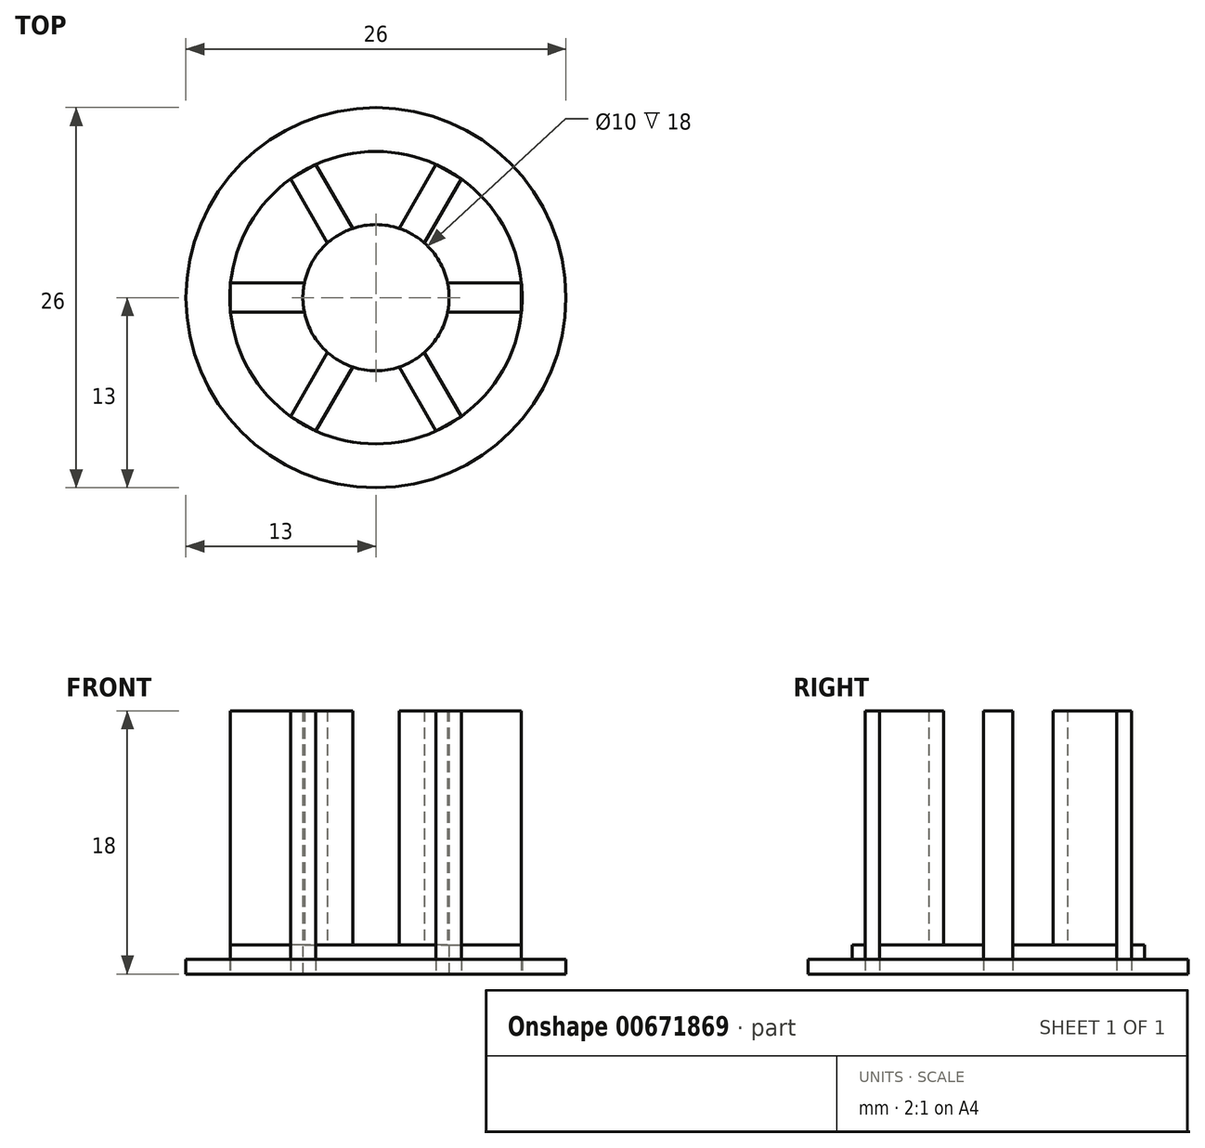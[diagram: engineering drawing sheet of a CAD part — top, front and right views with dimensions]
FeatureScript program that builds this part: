
annotation { "Feature Type Name" : "Feature", "Feature Type Description" : "" }
export const myFeature = defineFeature(function(context is Context, id is Id, definition is map)
    precondition{}
    {
        {
            var Q0;
            Q0=qCreatedBy(makeId("Top.planeOp"),FACE);
            var sketch = newSketch(context, id + "F0", { "sketchPlane" : qUnion([Q0])});
            skCircle(sketch, "E0", {"center": v(0, 0) * mm, "radius": 10 * mm});
            skCircle(sketch, "E1", {"center": v(0, 0) * mm, "radius": 13 * mm});
            skCircle(sketch, "E2", {"center": v(0, 0) * mm, "radius": 5 * mm});
            skLineSegment(sketch, "E3.bottom", {"start": v(9.95, -1) * mm, "end": v(4.9, -1) * mm});
            skLineSegment(sketch, "E3.top", {"start": v(9.95, 1) * mm, "end": v(4.9, 1) * mm});
            skLineSegment(sketch, "E3.left", {"start": v(9.95, -1) * mm, "end": v(9.95, 1) * mm});
            skLineSegment(sketch, "E3.right", {"start": v(4.9, -1) * mm, "end": v(4.9, 1) * mm});
            skPoint(sketch, "E3.middle", {"position": v(7.42, 0) * mm});
            skLineSegment(sketch, "E4.1.0", {"start": v(4.1, 9.12) * mm, "end": v(1.58, 4.74) * mm});
            skLineSegment(sketch, "E4.1.1", {"start": v(3.31, 3.74) * mm, "end": v(1.58, 4.74) * mm});
            skLineSegment(sketch, "E4.1.2", {"start": v(5.84, 8.12) * mm, "end": v(3.31, 3.74) * mm});
            skLineSegment(sketch, "E4.1.3", {"start": v(5.84, 8.12) * mm, "end": v(4.1, 9.12) * mm});
            skLineSegment(sketch, "E4.2.0", {"start": v(-5.84, 8.12) * mm, "end": v(-3.31, 3.74) * mm});
            skLineSegment(sketch, "E4.2.1", {"start": v(-1.58, 4.74) * mm, "end": v(-3.31, 3.74) * mm});
            skLineSegment(sketch, "E4.2.2", {"start": v(-4.1, 9.12) * mm, "end": v(-1.58, 4.74) * mm});
            skLineSegment(sketch, "E4.2.3", {"start": v(-4.1, 9.12) * mm, "end": v(-5.84, 8.12) * mm});
            skLineSegment(sketch, "E4.3.0", {"start": v(-9.95, -1) * mm, "end": v(-4.9, -1) * mm});
            skLineSegment(sketch, "E4.3.1", {"start": v(-4.9, 1) * mm, "end": v(-4.9, -1) * mm});
            skLineSegment(sketch, "E4.3.2", {"start": v(-9.95, 1) * mm, "end": v(-4.9, 1) * mm});
            skLineSegment(sketch, "E4.3.3", {"start": v(-9.95, 1) * mm, "end": v(-9.95, -1) * mm});
            skLineSegment(sketch, "E4.4.0", {"start": v(-4.1, -9.12) * mm, "end": v(-1.58, -4.74) * mm});
            skLineSegment(sketch, "E4.4.1", {"start": v(-3.31, -3.74) * mm, "end": v(-1.58, -4.74) * mm});
            skLineSegment(sketch, "E4.4.2", {"start": v(-5.84, -8.12) * mm, "end": v(-3.31, -3.74) * mm});
            skLineSegment(sketch, "E4.4.3", {"start": v(-5.84, -8.12) * mm, "end": v(-4.1, -9.12) * mm});
            skLineSegment(sketch, "E4.5.0", {"start": v(5.84, -8.12) * mm, "end": v(3.31, -3.74) * mm});
            skLineSegment(sketch, "E4.5.1", {"start": v(1.58, -4.74) * mm, "end": v(3.31, -3.74) * mm});
            skLineSegment(sketch, "E4.5.2", {"start": v(4.1, -9.12) * mm, "end": v(1.58, -4.74) * mm});
            skLineSegment(sketch, "E4.5.3", {"start": v(4.1, -9.12) * mm, "end": v(5.84, -8.12) * mm});
            skSolve(sketch);
        }
        {
            var Q0;
            Q0=makeQuery(id+"F0.imprint","IMPRINT",FACE,{"disambiguationData":[TD([[makeQuery(id+"F0.imprint","IMPRINT",EDGE,{"derivedFrom":sQuery(id+"F0.wireOp",EDGE,"E1")}),1.0]])]});
            extrude(context, id + "F1", {"entities" : qUnion([Q0]), "depth" : 1 * mm, "offsetDistance" : 25 * mm});
        }
        {
            var Q0;
            {var subQ0=sQuery(id+"F0.wireOp",EDGE,"E4.3.0");var subQ5=sQuery(id+"F0.wireOp",EDGE,"E2");var subQ6=makeQuery(id+"F0.imprint","INTERSECT",VERTEX,{"derivedFrom":[subQ5,subQ0]});Q0=makeQuery(id+"F0.imprint","IMPRINT",FACE,{"disambiguationData":[TD([[makeQuery(id+"F0.imprint","IMPRINT",EDGE,{"disambiguationData":[TD([[subQ6,-1.0]])],"derivedFrom":subQ5}),-1.0]])]});}
            var Q1;
            {var subQ5=sQuery(id+"F0.wireOp",EDGE,"E4.3.3");Q1=makeQuery(id+"F0.imprint","IMPRINT",FACE,{"disambiguationData":[TD([[makeQuery(id+"F0.imprint","IMPRINT",EDGE,{"derivedFrom":subQ5}),1.0]])]});}
            var Q2;
            {var subQ0=sQuery(id+"F0.wireOp",EDGE,"E4.2.0");var subQ5=sQuery(id+"F0.wireOp",EDGE,"E2");var subQ6=makeQuery(id+"F0.imprint","INTERSECT",VERTEX,{"derivedFrom":[subQ5,subQ0]});Q2=makeQuery(id+"F0.imprint","IMPRINT",FACE,{"disambiguationData":[TD([[makeQuery(id+"F0.imprint","IMPRINT",EDGE,{"disambiguationData":[TD([[subQ6,-1.0]])],"derivedFrom":subQ5}),-1.0]])]});}
            var Q3;
            {var subQ5=sQuery(id+"F0.wireOp",EDGE,"E4.2.3");Q3=makeQuery(id+"F0.imprint","IMPRINT",FACE,{"disambiguationData":[TD([[makeQuery(id+"F0.imprint","IMPRINT",EDGE,{"derivedFrom":subQ5}),1.0]])]});}
            var Q4;
            {var subQ0=sQuery(id+"F0.wireOp",EDGE,"E4.1.0");var subQ5=sQuery(id+"F0.wireOp",EDGE,"E2");var subQ6=makeQuery(id+"F0.imprint","INTERSECT",VERTEX,{"derivedFrom":[subQ5,subQ0]});Q4=makeQuery(id+"F0.imprint","IMPRINT",FACE,{"disambiguationData":[TD([[makeQuery(id+"F0.imprint","IMPRINT",EDGE,{"disambiguationData":[TD([[subQ6,-1.0]])],"derivedFrom":subQ5}),-1.0]])]});}
            var Q5;
            {var subQ3=sQuery(id+"F0.wireOp",EDGE,"E4.1.2");var subQ5=sQuery(id+"F0.wireOp",EDGE,"E2");var subQ6=makeQuery(id+"F0.imprint","INTERSECT",VERTEX,{"derivedFrom":[subQ5,subQ3]});Q5=makeQuery(id+"F0.imprint","IMPRINT",FACE,{"disambiguationData":[TD([[makeQuery(id+"F0.imprint","IMPRINT",EDGE,{"disambiguationData":[TD([[subQ6,1.0]])],"derivedFrom":subQ5}),-1.0]])]});}
            var Q6;
            {var subQ5=sQuery(id+"F0.wireOp",EDGE,"E3.left");Q6=makeQuery(id+"F0.imprint","IMPRINT",FACE,{"disambiguationData":[TD([[makeQuery(id+"F0.imprint","IMPRINT",EDGE,{"derivedFrom":subQ5}),1.0]])]});}
            var Q7;
            {var subQ5=sQuery(id+"F0.wireOp",EDGE,"E4.1.3");Q7=makeQuery(id+"F0.imprint","IMPRINT",FACE,{"disambiguationData":[TD([[makeQuery(id+"F0.imprint","IMPRINT",EDGE,{"derivedFrom":subQ5}),1.0]])]});}
            var Q8;
            {var subQ3=sQuery(id+"F0.wireOp",EDGE,"E4.5.0");var subQ5=sQuery(id+"F0.wireOp",EDGE,"E2");var subQ7=makeQuery(id+"F0.imprint","INTERSECT",VERTEX,{"derivedFrom":[subQ5,subQ3]});Q8=makeQuery(id+"F0.imprint","IMPRINT",FACE,{"disambiguationData":[TD([[makeQuery(id+"F0.imprint","IMPRINT",EDGE,{"disambiguationData":[TD([[subQ7,-1.0]])],"derivedFrom":subQ5}),-1.0]])]});}
            var Q9;
            {var subQ5=sQuery(id+"F0.wireOp",EDGE,"E4.5.3");Q9=makeQuery(id+"F0.imprint","IMPRINT",FACE,{"disambiguationData":[TD([[makeQuery(id+"F0.imprint","IMPRINT",EDGE,{"derivedFrom":subQ5}),1.0]])]});}
            var Q10;
            {var subQ0=sQuery(id+"F0.wireOp",EDGE,"E4.4.0");var subQ5=sQuery(id+"F0.wireOp",EDGE,"E2");var subQ7=makeQuery(id+"F0.imprint","INTERSECT",VERTEX,{"derivedFrom":[subQ5,subQ0]});Q10=makeQuery(id+"F0.imprint","IMPRINT",FACE,{"disambiguationData":[TD([[makeQuery(id+"F0.imprint","IMPRINT",EDGE,{"disambiguationData":[TD([[subQ7,-1.0]])],"derivedFrom":subQ5}),-1.0]])]});}
            var Q11;
            {var subQ5=sQuery(id+"F0.wireOp",EDGE,"E4.4.3");Q11=makeQuery(id+"F0.imprint","IMPRINT",FACE,{"disambiguationData":[TD([[makeQuery(id+"F0.imprint","IMPRINT",EDGE,{"derivedFrom":subQ5}),1.0]])]});}
            extrude(context, id + "F2", {"entities" : qUnion([Q0, Q1, Q2, Q3, Q4, Q5, Q6, Q7, Q8, Q9, Q10, Q11]), "operationType" : NewBodyOperationType.ADD, "depth" : 2 * mm, "offsetDistance" : 25 * mm});
        }
        {
            var Q0;
            {var subQ5=sQuery(id+"F0.wireOp",EDGE,"E4.1.3");Q0=makeQuery(id+"F0.imprint","IMPRINT",FACE,{"disambiguationData":[TD([[makeQuery(id+"F0.imprint","IMPRINT",EDGE,{"derivedFrom":subQ5}),1.0]])]});}
            var Q1;
            {var subQ5=sQuery(id+"F0.wireOp",EDGE,"E4.2.3");Q1=makeQuery(id+"F0.imprint","IMPRINT",FACE,{"disambiguationData":[TD([[makeQuery(id+"F0.imprint","IMPRINT",EDGE,{"derivedFrom":subQ5}),1.0]])]});}
            var Q2;
            {var subQ5=sQuery(id+"F0.wireOp",EDGE,"E4.3.3");Q2=makeQuery(id+"F0.imprint","IMPRINT",FACE,{"disambiguationData":[TD([[makeQuery(id+"F0.imprint","IMPRINT",EDGE,{"derivedFrom":subQ5}),1.0]])]});}
            var Q3;
            {var subQ5=sQuery(id+"F0.wireOp",EDGE,"E4.4.3");Q3=makeQuery(id+"F0.imprint","IMPRINT",FACE,{"disambiguationData":[TD([[makeQuery(id+"F0.imprint","IMPRINT",EDGE,{"derivedFrom":subQ5}),1.0]])]});}
            var Q4;
            {var subQ5=sQuery(id+"F0.wireOp",EDGE,"E4.5.3");Q4=makeQuery(id+"F0.imprint","IMPRINT",FACE,{"disambiguationData":[TD([[makeQuery(id+"F0.imprint","IMPRINT",EDGE,{"derivedFrom":subQ5}),1.0]])]});}
            var Q5;
            {var subQ5=sQuery(id+"F0.wireOp",EDGE,"E3.left");Q5=makeQuery(id+"F0.imprint","IMPRINT",FACE,{"disambiguationData":[TD([[makeQuery(id+"F0.imprint","IMPRINT",EDGE,{"derivedFrom":subQ5}),1.0]])]});}
            extrude(context, id + "F3", {"entities" : qUnion([Q0, Q1, Q2, Q3, Q4, Q5]), "operationType" : NewBodyOperationType.ADD, "depth" : 18 * mm, "offsetDistance" : 25 * mm});
        }
    });
